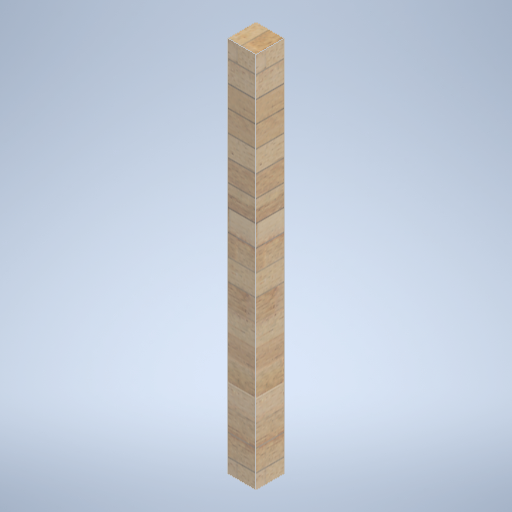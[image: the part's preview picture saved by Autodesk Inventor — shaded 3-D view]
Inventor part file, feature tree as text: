
AUTODESK INVENTOR PART (.ipt)
format: ipt  version: 2025.3 (Build 293356000, 356)  size: 302,080 bytes
history: native  units: mm
features: other x1, extrude x1, sketch x1
ambient origin geometry x8: Origin, YZ Plane, XZ Plane, XY Plane, X Axis, Y Axis, Z Axis, Center Point
bodies: Body1 (feature_tree)
feature tree (3):
  other  "Sólido1"
  extrude  "Extrusión1"  Depth=75.0mm
  sketch  "Boceto1"  dims[d0=75.0mm d1=75.0mm d2=1000.0mm d3=0.0mm]
